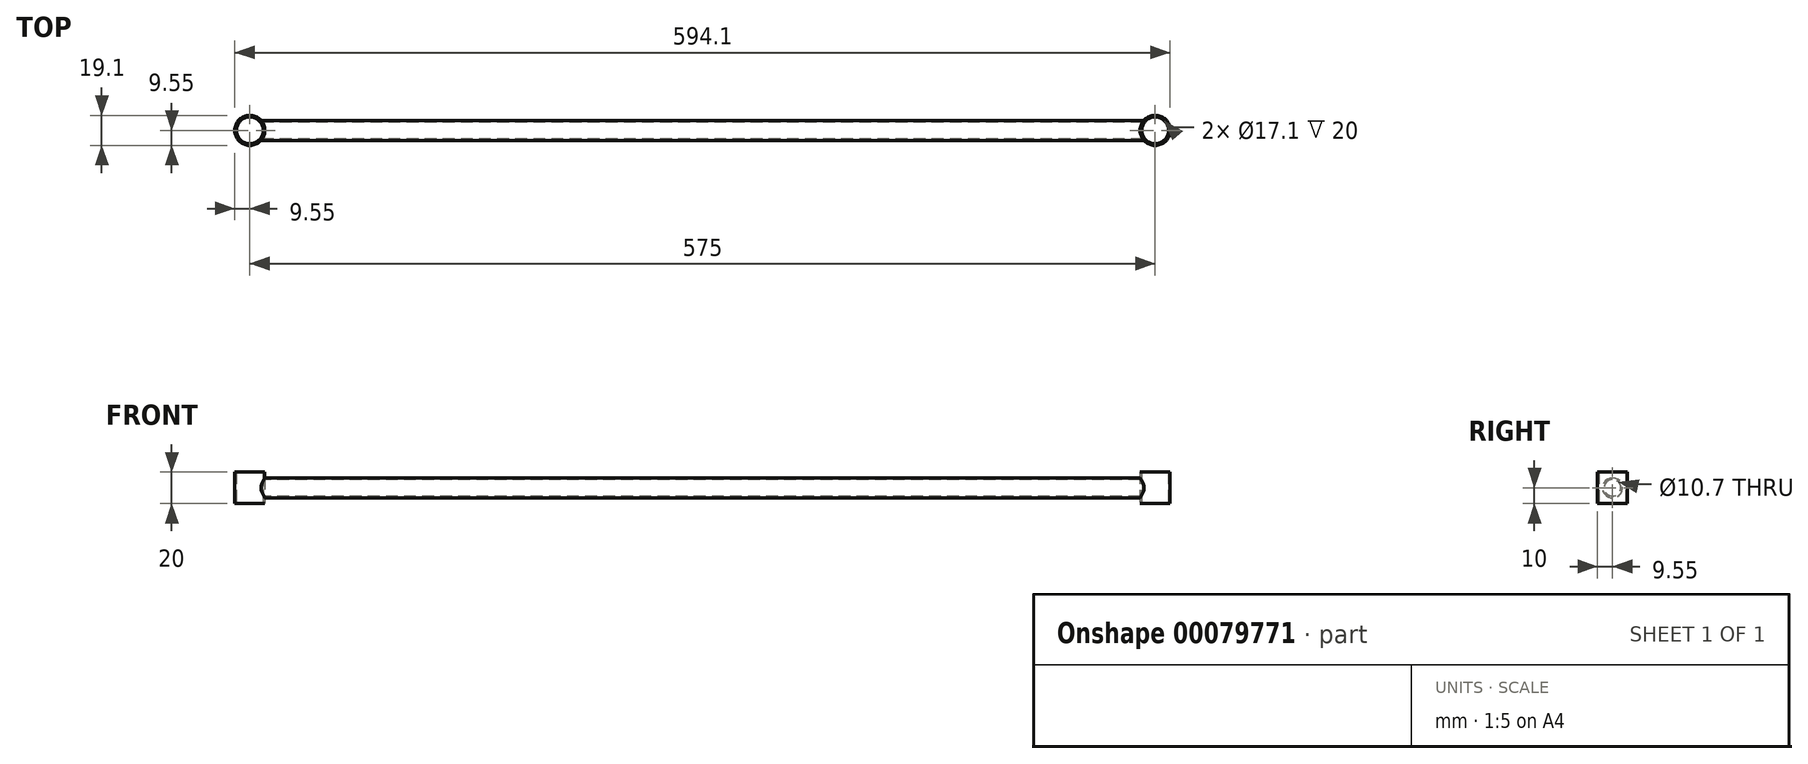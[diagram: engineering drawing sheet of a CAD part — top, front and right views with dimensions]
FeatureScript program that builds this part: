
annotation { "Feature Type Name" : "Feature", "Feature Type Description" : "" }
export const myFeature = defineFeature(function(context is Context, id is Id, definition is map)
    precondition{}
    {
        {
            var Q0;
            Q0=qCreatedBy(makeId("Top.planeOp"),FACE);
            var sketch = newSketch(context, id + "F0", { "sketchPlane" : qUnion([Q0])});
            skCircle(sketch, "E0", {"center": v(0, 0) * mm, "radius": 9.55 * mm});
            skCircle(sketch, "E1", {"center": v(0, 0) * mm, "radius": 8.55 * mm});
            skSolve(sketch);
        }
        {
            var Q0;
            Q0 = qSketchRegion(id + "F0", true);
            extrude(context, id + "F1", {"entities" : qUnion([Q0]), "endBound" : BoundingType.SYMMETRIC, "depth" : 20 * mm});
        }
        {
            var Q0;
            Q0=makeQuery(id+"F1.opExtrude","SWEPT_BODY",BODY,{"disambiguationData":[OSD([sQuery(id+"F0.wireOp",EDGE,"E0"),sQuery(id+"F0.wireOp",EDGE,"E1")])]});
            transform(context, id + "F2", {"entities" : qUnion([Q0]), "transformType" : TransformType.TRANSLATION_3D, "dx" : (575 / 2) * mm, "dy" : 0 * mm, "dz" : 0 * mm, "makeCopy" : false});
        }
        {
            var Q0;
            Q0=makeQuery(id+"F1.opExtrude","SWEPT_BODY",BODY,{"disambiguationData":[OSD([sQuery(id+"F0.wireOp",EDGE,"E0"),sQuery(id+"F0.wireOp",EDGE,"E1")])]});
            var Q1;
            Q1=qCreatedBy(makeId("Right.planeOp"),FACE);
            mirror(context, id + "F3", {"entities" : qUnion([Q0]), "mirrorPlane" : qUnion([Q1])});
        }
        {
            var Q0;
            Q0=qCreatedBy(makeId("Right.planeOp"),FACE);
            var sketch = newSketch(context, id + "F4", { "sketchPlane" : qUnion([Q0])});
            skCircle(sketch, "E2", {"center": v(0, 0) * mm, "radius": 6.35 * mm});
            skCircle(sketch, "E3", {"center": v(0, 0) * mm, "radius": 5.35 * mm});
            skSolve(sketch);
        }
        {
            var Q0;
            Q0 = qSketchRegion(id + "F4", true);
            var Q1;
            Q1=makeQuery(id+"F1.opExtrude","SWEPT_FACE",FACE,{"disambiguationData":[OSD([sQuery(id+"F0.wireOp",EDGE,"E0")])]});
            var Q2;
            Q2=makeQuery(id+"F3.opPattern","COPY",FACE,{"derivedFrom":makeQuery(id+"F1.opExtrude","SWEPT_FACE",FACE,{"disambiguationData":[OSD([sQuery(id+"F0.wireOp",EDGE,"E0")])]}),"instanceName":"1"});
            extrude(context, id + "F5", {"entities" : qUnion([Q0]), "endBound" : BoundingType.UP_TO_SURFACE, "endBoundEntityFace" : qUnion([Q1]), "depth" : 25 * mm, "hasSecondDirection" : true, "secondDirectionBound" : SecondDirectionBoundingType.UP_TO_SURFACE, "secondDirectionOppositeDirection" : true, "secondDirectionBoundEntityFace" : qUnion([Q2]), "secondDirectionDepth" : 25 * mm});
        }
    });
